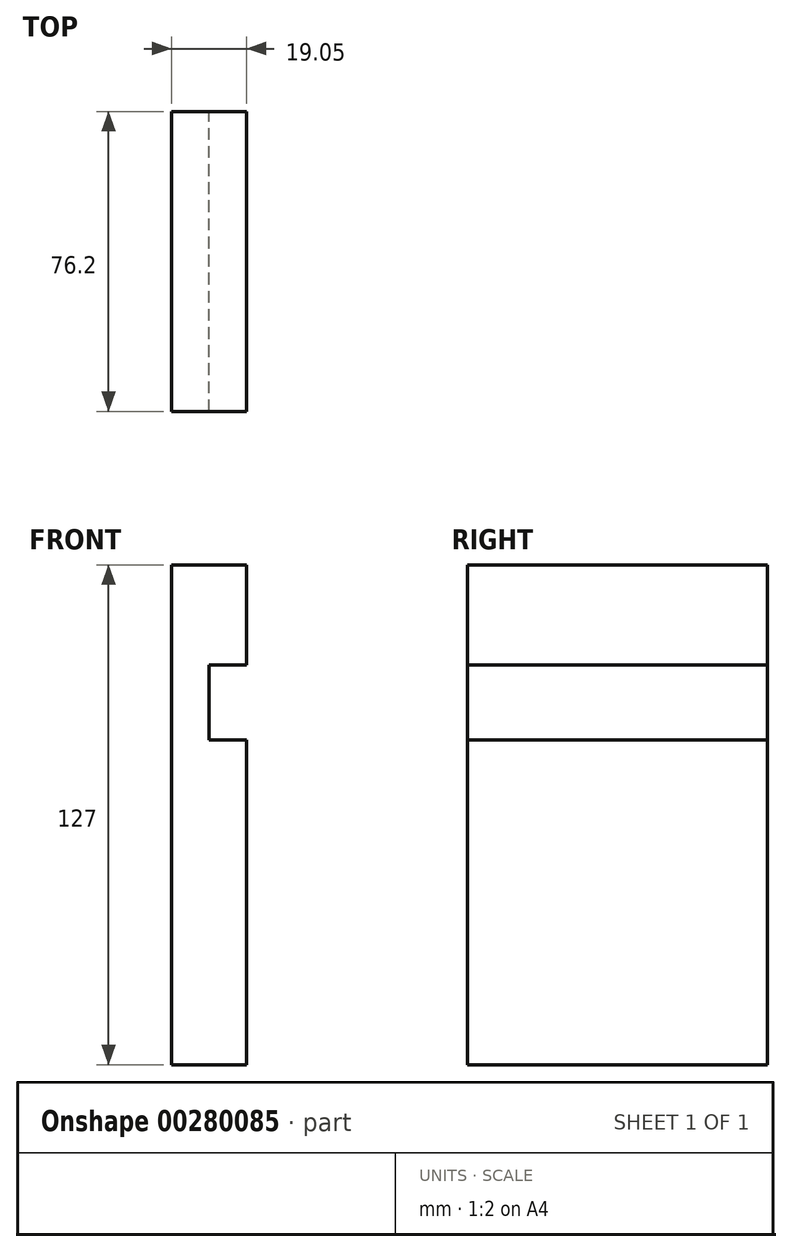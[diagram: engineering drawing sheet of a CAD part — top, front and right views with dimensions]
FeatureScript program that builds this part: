
annotation { "Feature Type Name" : "Feature", "Feature Type Description" : "" }
export const myFeature = defineFeature(function(context is Context, id is Id, definition is map)
    precondition{}
    {
        {
            var Q0;
            Q0=qCreatedBy(makeId("Front.planeOp"),FACE);
            var sketch = newSketch(context, id + "F0", { "sketchPlane" : qUnion([Q0])});
            skLineSegment(sketch, "E0", {"start": v(-76, 0) * mm, "end": v(-76, 127) * mm});
            skLineSegment(sketch, "E1", {"start": v(-76, 127) * mm, "end": v(-56.95, 127) * mm});
            skLineSegment(sketch, "E2", {"start": v(-56.95, 127) * mm, "end": v(-56.95, 101.6) * mm});
            skLineSegment(sketch, "E3", {"start": v(-56.95, 101.6) * mm, "end": v(-66.47, 101.6) * mm});
            skLineSegment(sketch, "E4", {"start": v(-66.47, 101.6) * mm, "end": v(-66.47, 82.55) * mm});
            skLineSegment(sketch, "E5", {"start": v(-66.47, 82.55) * mm, "end": v(-56.95, 82.55) * mm});
            skLineSegment(sketch, "E6", {"start": v(-56.95, 82.55) * mm, "end": v(-56.95, 0) * mm});
            skLineSegment(sketch, "E7", {"start": v(-56.95, 0) * mm, "end": v(-76, 0) * mm});
            skSolve(sketch);
        }
        {
            var Q0;
            Q0 = qSketchRegion(id + "F0", true);
            extrude(context, id + "F1", {"entities" : qUnion([Q0]), "depth" : 76.2 * mm});
        }
    });
